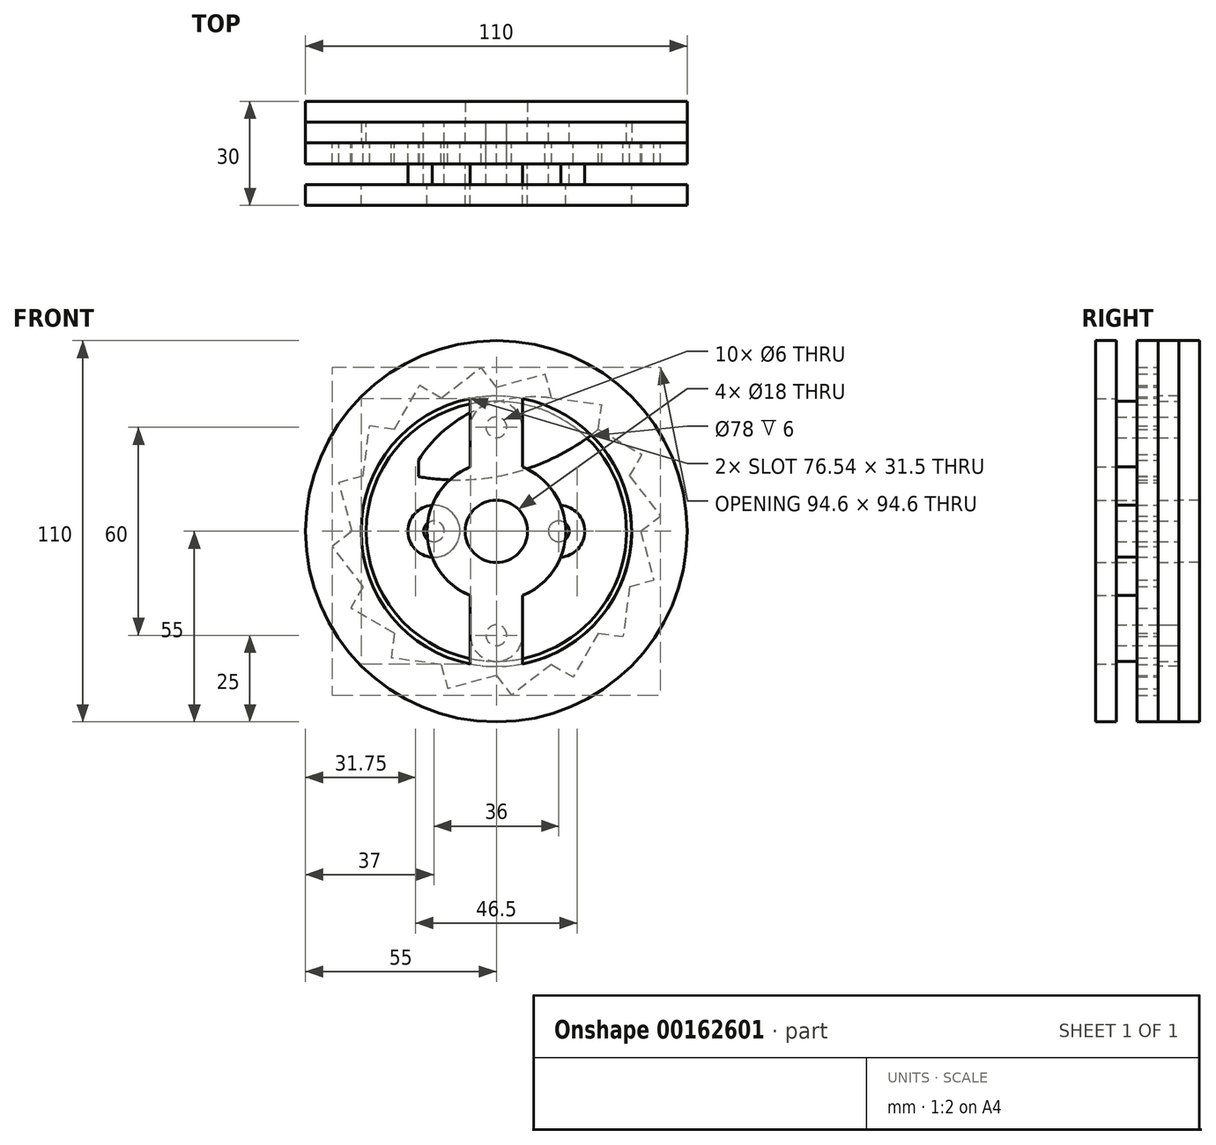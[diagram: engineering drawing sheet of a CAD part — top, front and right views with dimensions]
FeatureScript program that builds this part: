
annotation { "Feature Type Name" : "Feature", "Feature Type Description" : "" }
export const myFeature = defineFeature(function(context is Context, id is Id, definition is map)
    precondition{}
    {
        {
            var Q0;
            Q0=qCreatedBy(makeId("Right.planeOp"),FACE);
            var sketch = newSketch(context, id + "F0", { "sketchPlane" : qUnion([Q0])});
            skLineSegment(sketch, "E0", {"start": v(0, 0) * mm, "end": v(-98.62, 0) * mm, "construction": true});
            skSolve(sketch);
        }
        {
            var Q0;
            Q0=qCreatedBy(makeId("Front.planeOp"),FACE);
            var sketch = newSketch(context, id + "F1", { "sketchPlane" : qUnion([Q0])});
            skCircle(sketch, "E1", {"center": v(0, 0) * mm, "radius": 9 * mm});
            skCircle(sketch, "E2", {"center": v(0, 0) * mm, "radius": 37.5 * mm});
            skCircle(sketch, "E3", {"center": v(0, 30) * mm, "radius": 3 * mm});
            skCircle(sketch, "E4", {"center": v(0, -30) * mm, "radius": 3 * mm});
            skCircle(sketch, "E5", {"center": v(18, 0) * mm, "radius": 3 * mm});
            skCircle(sketch, "E6", {"center": v(-18, 0) * mm, "radius": 3 * mm});
            skSolve(sketch);
        }
        {
            var Q0;
            Q0=qSketchRegion(id+"F1",true);
            extrude(context, id + "F2", {"entities" : qUnion([Q0]), "depth" : 6 * mm});
        }
        {
            var Q0;
            Q0=makeQuery(id+"F2.opExtrude","CAP_FACE",FACE,{"disambiguationData":[OSD([sQuery(id+"F1.wireOp",EDGE,"E1"),sQuery(id+"F1.wireOp",EDGE,"E2"),sQuery(id+"F1.wireOp",EDGE,"E3"),sQuery(id+"F1.wireOp",EDGE,"E4")])],"isStart":false});
            var sketch = newSketch(context, id + "F3", { "sketchPlane" : qUnion([Q0])});
            skPoint(sketch, "E7.center", {"position": v(0, 0) * mm});
            skCircle(sketch, "E8", {"center": v(0, 0) * mm, "radius": 39 * mm, "construction": true});
            skCircle(sketch, "E9", {"center": v(0, 0) * mm, "radius": 47.5 * mm, "construction": true});
            skCircle(sketch, "E10", {"center": v(0, 0) * mm, "radius": 55 * mm});
            skLineSegment(sketch, "E11", {"start": v(0, 0) * mm, "end": v(47.5, 0) * mm, "construction": true});
            skLineSegment(sketch, "E12", {"start": v(0, 0) * mm, "end": v(43.88, 18.18) * mm, "construction": true});
            skLineSegment(sketch, "E13", {"start": v(0, 0) * mm, "end": v(33.59, 33.59) * mm, "construction": true});
            skLineSegment(sketch, "E14", {"start": v(38.43, 15.92) * mm, "end": v(47.3, 4.38) * mm});
            skLineSegment(sketch, "E15", {"start": v(41.6, 0) * mm, "end": v(47.3, 4.38) * mm});
            skLineSegment(sketch, "E16", {"start": v(0, 0) * mm, "end": v(47.3, 4.38) * mm, "construction": true});
            skLineSegment(sketch, "E17.1.0", {"start": v(29.41, 29.41) * mm, "end": v(42.02, 22.15) * mm});
            skLineSegment(sketch, "E17.1.1", {"start": v(38.43, 15.92) * mm, "end": v(42.02, 22.15) * mm});
            skLineSegment(sketch, "E17.2.0", {"start": v(15.92, 38.43) * mm, "end": v(30.35, 36.54) * mm});
            skLineSegment(sketch, "E17.2.1", {"start": v(29.41, 29.41) * mm, "end": v(30.35, 36.54) * mm});
            skLineSegment(sketch, "E17.3.0", {"start": v(0, 41.6) * mm, "end": v(14.05, 45.37) * mm});
            skLineSegment(sketch, "E17.3.1", {"start": v(15.92, 38.43) * mm, "end": v(14.05, 45.37) * mm});
            skLineSegment(sketch, "E17.4.0", {"start": v(-15.92, 38.43) * mm, "end": v(-4.38, 47.3) * mm});
            skLineSegment(sketch, "E17.4.1", {"start": v(0, 41.6) * mm, "end": v(-4.38, 47.3) * mm});
            skLineSegment(sketch, "E17.5.0", {"start": v(-29.41, 29.41) * mm, "end": v(-22.15, 42.02) * mm});
            skLineSegment(sketch, "E17.5.1", {"start": v(-15.92, 38.43) * mm, "end": v(-22.15, 42.02) * mm});
            skLineSegment(sketch, "E17.6.0", {"start": v(-38.43, 15.92) * mm, "end": v(-36.54, 30.35) * mm});
            skLineSegment(sketch, "E17.6.1", {"start": v(-29.41, 29.41) * mm, "end": v(-36.54, 30.35) * mm});
            skLineSegment(sketch, "E17.7.0", {"start": v(-41.6, 0) * mm, "end": v(-45.37, 14.05) * mm});
            skLineSegment(sketch, "E17.7.1", {"start": v(-38.43, 15.92) * mm, "end": v(-45.37, 14.05) * mm});
            skLineSegment(sketch, "E17.8.0", {"start": v(-38.43, -15.92) * mm, "end": v(-47.3, -4.38) * mm});
            skLineSegment(sketch, "E17.8.1", {"start": v(-41.6, 0) * mm, "end": v(-47.3, -4.38) * mm});
            skLineSegment(sketch, "E17.9.0", {"start": v(-29.41, -29.41) * mm, "end": v(-42.02, -22.15) * mm});
            skLineSegment(sketch, "E17.9.1", {"start": v(-38.43, -15.92) * mm, "end": v(-42.02, -22.15) * mm});
            skLineSegment(sketch, "E17.10.0", {"start": v(-15.92, -38.43) * mm, "end": v(-30.35, -36.54) * mm});
            skLineSegment(sketch, "E17.10.1", {"start": v(-29.41, -29.41) * mm, "end": v(-30.35, -36.54) * mm});
            skLineSegment(sketch, "E17.11.0", {"start": v(0, -41.6) * mm, "end": v(-14.05, -45.37) * mm});
            skLineSegment(sketch, "E17.11.1", {"start": v(-15.92, -38.43) * mm, "end": v(-14.05, -45.37) * mm});
            skLineSegment(sketch, "E17.12.0", {"start": v(15.92, -38.43) * mm, "end": v(4.38, -47.3) * mm});
            skLineSegment(sketch, "E17.12.1", {"start": v(0, -41.6) * mm, "end": v(4.38, -47.3) * mm});
            skLineSegment(sketch, "E17.13.0", {"start": v(29.41, -29.41) * mm, "end": v(22.15, -42.02) * mm});
            skLineSegment(sketch, "E17.13.1", {"start": v(15.92, -38.43) * mm, "end": v(22.15, -42.02) * mm});
            skLineSegment(sketch, "E17.14.0", {"start": v(38.43, -15.92) * mm, "end": v(36.54, -30.35) * mm});
            skLineSegment(sketch, "E17.14.1", {"start": v(29.41, -29.41) * mm, "end": v(36.54, -30.35) * mm});
            skLineSegment(sketch, "E17.15.0", {"start": v(41.6, 0) * mm, "end": v(45.37, -14.05) * mm});
            skLineSegment(sketch, "E17.15.1", {"start": v(38.43, -15.92) * mm, "end": v(45.37, -14.05) * mm});
            skSolve(sketch);
        }
        {
            var Q0;
            Q0=qSketchRegion(id+"F3",true);
            extrude(context, id + "F4", {"entities" : qUnion([Q0]), "depth" : 6 * mm});
        }
        {
            var Q0;
            Q0=makeQuery(id+"F2.opExtrude","CAP_FACE",FACE,{"disambiguationData":[OSD([sQuery(id+"F1.wireOp",EDGE,"E1"),sQuery(id+"F1.wireOp",EDGE,"E2"),sQuery(id+"F1.wireOp",EDGE,"E3"),sQuery(id+"F1.wireOp",EDGE,"E4")])],"isStart":false});
            var sketch = newSketch(context, id + "F5", { "sketchPlane" : qUnion([Q0])});
            skCircle(sketch, "E18", {"center": v(0, 30) * mm, "radius": 3 * mm});
            skLineSegment(sketch, "E19", {"start": v(30.35, 36.54) * mm, "end": v(15.92, 38.43) * mm});
            skLineSegment(sketch, "E20.0", {"start": v(29.41, 29.41) * mm, "end": v(30.35, 36.54) * mm});
            skLineSegment(sketch, "E21", {"start": v(-22.48, 15.78) * mm, "end": v(-22.48, 20.47) * mm});
            skArc(sketch, "E22", {"start": v(-22.48, 15.78) * mm, "mid": v(4.97, 16.88) * mm, "end": v(29.41, 29.41) * mm});
            skArc(sketch, "E23", {"start": v(15.92, 38.43) * mm, "mid": v(-5.9, 35.05) * mm, "end": v(-22.48, 20.47) * mm});
            skSolve(sketch);
        }
        {
            var Q0;
            Q0=qSketchRegion(id+"F5",true);
            extrude(context, id + "F6", {"entities" : qUnion([Q0]), "depth" : 6 * mm});
        }
        {
            var Q0;
            Q0=qCreatedBy(makeId("Front.planeOp"),FACE);
            var sketch = newSketch(context, id + "F7", { "sketchPlane" : qUnion([Q0])});
            skCircle(sketch, "E24.0", {"center": v(0, -30) * mm, "radius": 3 * mm});
            skSolve(sketch);
        }
        {
            var Q0;
            Q0=qSketchRegion(id+"F7",true);
            extrude(context, id + "F8", {"entities" : qUnion([Q0]), "depth" : 18 * mm});
        }
        {
            var Q0;
            Q0=makeQuery(id+"F4.opExtrude","CAP_FACE",FACE,{"disambiguationData":[OSD([sQuery(id+"F3.wireOp",EDGE,"E10"),sQuery(id+"F3.wireOp",EDGE,"E14"),sQuery(id+"F3.wireOp",EDGE,"E15"),sQuery(id+"F3.wireOp",EDGE,"261d85d0-3812-4bcc-8ed8-0c975b53ec12.1.0"),sQuery(id+"F3.wireOp",EDGE,"261d85d0-3812-4bcc-8ed8-0c975b53ec12.1.1"),sQuery(id+"F3.wireOp",EDGE,"261d85d0-3812-4bcc-8ed8-0c975b53ec12.2.0"),sQuery(id+"F3.wireOp",EDGE,"261d85d0-3812-4bcc-8ed8-0c975b53ec12.2.1"),sQuery(id+"F3.wireOp",EDGE,"261d85d0-3812-4bcc-8ed8-0c975b53ec12.3.0"),sQuery(id+"F3.wireOp",EDGE,"261d85d0-3812-4bcc-8ed8-0c975b53ec12.3.1"),sQuery(id+"F3.wireOp",EDGE,"261d85d0-3812-4bcc-8ed8-0c975b53ec12.4.0"),sQuery(id+"F3.wireOp",EDGE,"261d85d0-3812-4bcc-8ed8-0c975b53ec12.4.1"),sQuery(id+"F3.wireOp",EDGE,"261d85d0-3812-4bcc-8ed8-0c975b53ec12.5.0"),sQuery(id+"F3.wireOp",EDGE,"261d85d0-3812-4bcc-8ed8-0c975b53ec12.5.1"),sQuery(id+"F3.wireOp",EDGE,"261d85d0-3812-4bcc-8ed8-0c975b53ec12.6.0"),sQuery(id+"F3.wireOp",EDGE,"261d85d0-3812-4bcc-8ed8-0c975b53ec12.6.1"),sQuery(id+"F3.wireOp",EDGE,"261d85d0-3812-4bcc-8ed8-0c975b53ec12.7.0"),sQuery(id+"F3.wireOp",EDGE,"261d85d0-3812-4bcc-8ed8-0c975b53ec12.7.1"),sQuery(id+"F3.wireOp",EDGE,"261d85d0-3812-4bcc-8ed8-0c975b53ec12.8.0"),sQuery(id+"F3.wireOp",EDGE,"261d85d0-3812-4bcc-8ed8-0c975b53ec12.8.1"),sQuery(id+"F3.wireOp",EDGE,"261d85d0-3812-4bcc-8ed8-0c975b53ec12.9.0"),sQuery(id+"F3.wireOp",EDGE,"261d85d0-3812-4bcc-8ed8-0c975b53ec12.9.1"),sQuery(id+"F3.wireOp",EDGE,"261d85d0-3812-4bcc-8ed8-0c975b53ec12.10.0"),sQuery(id+"F3.wireOp",EDGE,"261d85d0-3812-4bcc-8ed8-0c975b53ec12.10.1"),sQuery(id+"F3.wireOp",EDGE,"261d85d0-3812-4bcc-8ed8-0c975b53ec12.11.0"),sQuery(id+"F3.wireOp",EDGE,"261d85d0-3812-4bcc-8ed8-0c975b53ec12.11.1"),sQuery(id+"F3.wireOp",EDGE,"261d85d0-3812-4bcc-8ed8-0c975b53ec12.12.0"),sQuery(id+"F3.wireOp",EDGE,"261d85d0-3812-4bcc-8ed8-0c975b53ec12.12.1"),sQuery(id+"F3.wireOp",EDGE,"261d85d0-3812-4bcc-8ed8-0c975b53ec12.13.0"),sQuery(id+"F3.wireOp",EDGE,"261d85d0-3812-4bcc-8ed8-0c975b53ec12.13.1"),sQuery(id+"F3.wireOp",EDGE,"261d85d0-3812-4bcc-8ed8-0c975b53ec12.14.0"),sQuery(id+"F3.wireOp",EDGE,"261d85d0-3812-4bcc-8ed8-0c975b53ec12.14.1"),sQuery(id+"F3.wireOp",EDGE,"261d85d0-3812-4bcc-8ed8-0c975b53ec12.15.0"),sQuery(id+"F3.wireOp",EDGE,"261d85d0-3812-4bcc-8ed8-0c975b53ec12.15.1")])],"isStart":true});
            var sketch = newSketch(context, id + "F9", { "sketchPlane" : qUnion([Q0])});
            skCircle(sketch, "E25", {"center": v(0, 0) * mm, "radius": 55 * mm});
            skCircle(sketch, "E26", {"center": v(0, 0) * mm, "radius": 39 * mm});
            skSolve(sketch);
        }
        {
            var Q0;
            Q0=qSketchRegion(id+"F9",true);
            extrude(context, id + "F10", {"entities" : qUnion([Q0]), "depth" : 6 * mm});
        }
        {
            var Q0;
            Q0=makeQuery(id+"F10.opExtrude","CAP_FACE",FACE,{"disambiguationData":[OSD([sQuery(id+"F9.wireOp",EDGE,"E25"),sQuery(id+"F9.wireOp",EDGE,"E26")])],"isStart":false});
            var sketch = newSketch(context, id + "F11", { "sketchPlane" : qUnion([Q0])});
            skCircle(sketch, "E27", {"center": v(0, 0) * mm, "radius": 9 * mm});
            skCircle(sketch, "E28", {"center": v(0, 0) * mm, "radius": 55 * mm});
            skSolve(sketch);
        }
        {
            var Q0;
            Q0=qSketchRegion(id+"F11",true);
            extrude(context, id + "F12", {"entities" : qUnion([Q0]), "depth" : 6 * mm});
        }
        {
            var Q0;
            Q0=makeQuery(id+"F4.opExtrude","CAP_FACE",FACE,{"disambiguationData":[OSD([sQuery(id+"F3.wireOp",EDGE,"E10"),sQuery(id+"F3.wireOp",EDGE,"E14"),sQuery(id+"F3.wireOp",EDGE,"E15"),sQuery(id+"F3.wireOp",EDGE,"261d85d0-3812-4bcc-8ed8-0c975b53ec12.1.0"),sQuery(id+"F3.wireOp",EDGE,"261d85d0-3812-4bcc-8ed8-0c975b53ec12.1.1"),sQuery(id+"F3.wireOp",EDGE,"261d85d0-3812-4bcc-8ed8-0c975b53ec12.2.0"),sQuery(id+"F3.wireOp",EDGE,"261d85d0-3812-4bcc-8ed8-0c975b53ec12.2.1"),sQuery(id+"F3.wireOp",EDGE,"261d85d0-3812-4bcc-8ed8-0c975b53ec12.3.0"),sQuery(id+"F3.wireOp",EDGE,"261d85d0-3812-4bcc-8ed8-0c975b53ec12.3.1"),sQuery(id+"F3.wireOp",EDGE,"261d85d0-3812-4bcc-8ed8-0c975b53ec12.4.0"),sQuery(id+"F3.wireOp",EDGE,"261d85d0-3812-4bcc-8ed8-0c975b53ec12.4.1"),sQuery(id+"F3.wireOp",EDGE,"261d85d0-3812-4bcc-8ed8-0c975b53ec12.5.0"),sQuery(id+"F3.wireOp",EDGE,"261d85d0-3812-4bcc-8ed8-0c975b53ec12.5.1"),sQuery(id+"F3.wireOp",EDGE,"261d85d0-3812-4bcc-8ed8-0c975b53ec12.6.0"),sQuery(id+"F3.wireOp",EDGE,"261d85d0-3812-4bcc-8ed8-0c975b53ec12.6.1"),sQuery(id+"F3.wireOp",EDGE,"261d85d0-3812-4bcc-8ed8-0c975b53ec12.7.0"),sQuery(id+"F3.wireOp",EDGE,"261d85d0-3812-4bcc-8ed8-0c975b53ec12.7.1"),sQuery(id+"F3.wireOp",EDGE,"261d85d0-3812-4bcc-8ed8-0c975b53ec12.8.0"),sQuery(id+"F3.wireOp",EDGE,"261d85d0-3812-4bcc-8ed8-0c975b53ec12.8.1"),sQuery(id+"F3.wireOp",EDGE,"261d85d0-3812-4bcc-8ed8-0c975b53ec12.9.0"),sQuery(id+"F3.wireOp",EDGE,"261d85d0-3812-4bcc-8ed8-0c975b53ec12.9.1"),sQuery(id+"F3.wireOp",EDGE,"261d85d0-3812-4bcc-8ed8-0c975b53ec12.10.0"),sQuery(id+"F3.wireOp",EDGE,"261d85d0-3812-4bcc-8ed8-0c975b53ec12.10.1"),sQuery(id+"F3.wireOp",EDGE,"261d85d0-3812-4bcc-8ed8-0c975b53ec12.11.0"),sQuery(id+"F3.wireOp",EDGE,"261d85d0-3812-4bcc-8ed8-0c975b53ec12.11.1"),sQuery(id+"F3.wireOp",EDGE,"261d85d0-3812-4bcc-8ed8-0c975b53ec12.12.0"),sQuery(id+"F3.wireOp",EDGE,"261d85d0-3812-4bcc-8ed8-0c975b53ec12.12.1"),sQuery(id+"F3.wireOp",EDGE,"261d85d0-3812-4bcc-8ed8-0c975b53ec12.13.0"),sQuery(id+"F3.wireOp",EDGE,"261d85d0-3812-4bcc-8ed8-0c975b53ec12.13.1"),sQuery(id+"F3.wireOp",EDGE,"261d85d0-3812-4bcc-8ed8-0c975b53ec12.14.0"),sQuery(id+"F3.wireOp",EDGE,"261d85d0-3812-4bcc-8ed8-0c975b53ec12.14.1"),sQuery(id+"F3.wireOp",EDGE,"261d85d0-3812-4bcc-8ed8-0c975b53ec12.15.0"),sQuery(id+"F3.wireOp",EDGE,"261d85d0-3812-4bcc-8ed8-0c975b53ec12.15.1")])],"isStart":false});
            var sketch = newSketch(context, id + "F13", { "sketchPlane" : qUnion([Q0])});
            skArc(sketch, "E29", {"start": v(7.5, 30) * mm, "mid": v(0, 37.5) * mm, "end": v(-7.5, 30) * mm});
            skArc(sketch, "E30", {"start": v(-7.5, -30) * mm, "mid": v(0, -37.5) * mm, "end": v(7.5, -30) * mm});
            skArc(sketch, "E31", {"start": v(-18.55, 7.48) * mm, "mid": v(-25.5, 0) * mm, "end": v(-18.55, -7.48) * mm});
            skArc(sketch, "E32", {"start": v(18.55, -7.48) * mm, "mid": v(25.5, 0) * mm, "end": v(18.55, 7.48) * mm});
            skArc(sketch, "E33", {"start": v(-7.5, 18.54) * mm, "mid": v(-14.15, 14.13) * mm, "end": v(-18.55, 7.48) * mm});
            skLineSegment(sketch, "E34", {"start": v(7.5, 30) * mm, "end": v(7.5, 18.54) * mm});
            skLineSegment(sketch, "E35", {"start": v(-7.5, 30) * mm, "end": v(-7.5, 18.54) * mm});
            skLineSegment(sketch, "E36.trimOffspring", {"start": v(-7.5, -18.54) * mm, "end": v(-7.5, -30) * mm});
            skLineSegment(sketch, "E37.trimOffspring", {"start": v(7.5, -18.54) * mm, "end": v(7.5, -30) * mm});
            skArc(sketch, "E38.trimOffspring", {"start": v(7.5, -18.54) * mm, "mid": v(14.15, -14.13) * mm, "end": v(18.55, -7.48) * mm});
            skArc(sketch, "E39.trimOffspring", {"start": v(-18.55, -7.48) * mm, "mid": v(-14.15, -14.13) * mm, "end": v(-7.5, -18.54) * mm});
            skArc(sketch, "E40.trimOffspring", {"start": v(18.55, 7.48) * mm, "mid": v(14.15, 14.13) * mm, "end": v(7.5, 18.54) * mm});
            skCircle(sketch, "E41", {"center": v(0, 0) * mm, "radius": 9 * mm});
            skCircle(sketch, "E42", {"center": v(0, 30) * mm, "radius": 3 * mm});
            skCircle(sketch, "E43", {"center": v(18, 0) * mm, "radius": 3 * mm});
            skCircle(sketch, "E44", {"center": v(-18, 0) * mm, "radius": 3 * mm});
            skCircle(sketch, "E45", {"center": v(0, -30) * mm, "radius": 3 * mm});
            skSolve(sketch);
        }
        {
            var Q0;
            Q0=qSketchRegion(id+"F13",true);
            extrude(context, id + "F14", {"entities" : qUnion([Q0]), "depth" : 6 * mm});
        }
        {
            var Q0;
            Q0=makeQuery(id+"F14.opExtrude","CAP_FACE",FACE,{"disambiguationData":[OSD([sQuery(id+"F13.wireOp",EDGE,"E29"),sQuery(id+"F13.wireOp",EDGE,"E30"),sQuery(id+"F13.wireOp",EDGE,"E31"),sQuery(id+"F13.wireOp",EDGE,"E32"),sQuery(id+"F13.wireOp",EDGE,"E33"),sQuery(id+"F13.wireOp",EDGE,"E34"),sQuery(id+"F13.wireOp",EDGE,"E35"),sQuery(id+"F13.wireOp",EDGE,"E36.trimOffspring"),sQuery(id+"F13.wireOp",EDGE,"E37.trimOffspring"),sQuery(id+"F13.wireOp",EDGE,"E38.trimOffspring"),sQuery(id+"F13.wireOp",EDGE,"E39.trimOffspring"),sQuery(id+"F13.wireOp",EDGE,"E40.trimOffspring"),sQuery(id+"F13.wireOp",EDGE,"E41"),sQuery(id+"F13.wireOp",EDGE,"E42"),sQuery(id+"F13.wireOp",EDGE,"E43"),sQuery(id+"F13.wireOp",EDGE,"E44"),sQuery(id+"F13.wireOp",EDGE,"E45")])],"isStart":false});
            var sketch = newSketch(context, id + "F15", { "sketchPlane" : qUnion([Q0])});
            skCircle(sketch, "E46", {"center": v(0, 0) * mm, "radius": 55 * mm});
            skArc(sketch, "E47", {"start": v(-7.5, 38.27) * mm, "mid": v(-39, 0) * mm, "end": v(-7.5, -38.27) * mm});
            skArc(sketch, "E48", {"start": v(-7.5, 18.54) * mm, "mid": v(-20, 0) * mm, "end": v(-7.5, -18.54) * mm});
            skCircle(sketch, "E49", {"center": v(0, 0) * mm, "radius": 9 * mm});
            skLineSegment(sketch, "E50", {"start": v(-7.5, 18.54) * mm, "end": v(-7.5, 38.27) * mm});
            skLineSegment(sketch, "E51", {"start": v(7.5, 18.54) * mm, "end": v(7.5, 38.27) * mm});
            skLineSegment(sketch, "E52", {"start": v(-7.5, -18.54) * mm, "end": v(-7.5, -38.27) * mm});
            skLineSegment(sketch, "E53", {"start": v(7.5, -18.54) * mm, "end": v(7.5, -38.27) * mm});
            skArc(sketch, "E54.trimOffspring", {"start": v(7.5, -18.54) * mm, "mid": v(20, 0) * mm, "end": v(7.5, 18.54) * mm});
            skArc(sketch, "E55.trimOffspring", {"start": v(7.5, -38.27) * mm, "mid": v(39, 0) * mm, "end": v(7.5, 38.27) * mm});
            skSolve(sketch);
        }
        {
            var Q0;
            Q0=qSketchRegion(id+"F15",true);
            extrude(context, id + "F16", {"entities" : qUnion([Q0]), "depth" : 6 * mm});
        }
        {
            var Q0;
            Q0=makeQuery(id+"F2.opExtrude","CAP_FACE",FACE,{"disambiguationData":[OSD([sQuery(id+"F1.wireOp",EDGE,"E1"),sQuery(id+"F1.wireOp",EDGE,"E2"),sQuery(id+"F1.wireOp",EDGE,"E3"),sQuery(id+"F1.wireOp",EDGE,"E4"),sQuery(id+"F1.wireOp",EDGE,"E5"),sQuery(id+"F1.wireOp",EDGE,"E6")])],"isStart":false});
            var sketch = newSketch(context, id + "F17", { "sketchPlane" : qUnion([Q0])});
            skCircle(sketch, "E56", {"center": v(-18, 0) * mm, "radius": 3 * mm});
            skCircle(sketch, "E57", {"center": v(-18, 0) * mm, "radius": 7.5 * mm});
            skSolve(sketch);
        }
        {
            var Q0;
            Q0=qSketchRegion(id+"F17",true);
            extrude(context, id + "F18", {"entities" : qUnion([Q0]), "depth" : 6 * mm});
        }
    });
